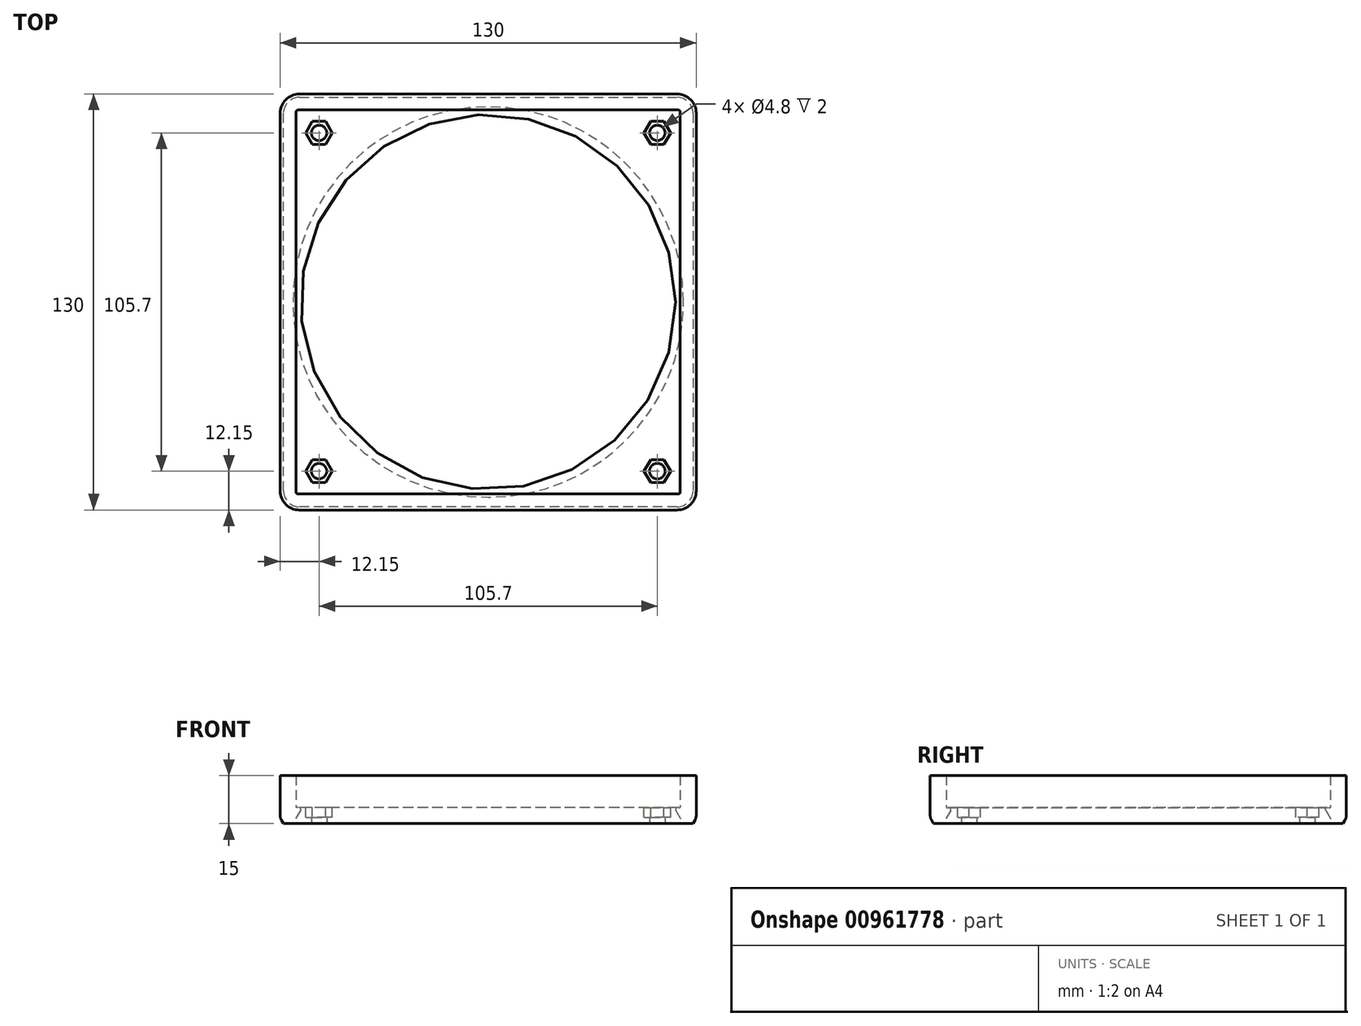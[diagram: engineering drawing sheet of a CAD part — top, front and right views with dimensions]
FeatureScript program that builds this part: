
annotation { "Feature Type Name" : "Feature", "Feature Type Description" : "" }
export const myFeature = defineFeature(function(context is Context, id is Id, definition is map)
    precondition{}
    {
        {
            var Q0;
            Q0=qCreatedBy(makeId("Top.planeOp"),FACE);
            var sketch = newSketch(context, id + "F0", { "sketchPlane" : qUnion([Q0])});
            skLineSegment(sketch, "E0.bottom", {"start": v(60, -60) * mm, "end": v(-60, -60) * mm});
            skLineSegment(sketch, "E0.top", {"start": v(60, 60) * mm, "end": v(-60, 60) * mm});
            skLineSegment(sketch, "E0.left", {"start": v(60, -60) * mm, "end": v(60, 60) * mm});
            skLineSegment(sketch, "E0.right", {"start": v(-60, -60) * mm, "end": v(-60, 60) * mm});
            skPoint(sketch, "E0.middle", {"position": v(0, 0) * mm});
            skLineSegment(sketch, "E1.0", {"start": v(65, -60) * mm, "end": v(65, 65) * mm});
            skLineSegment(sketch, "E1.1", {"start": v(65, 65) * mm, "end": v(-65, 65) * mm});
            skLineSegment(sketch, "E1.2", {"start": v(-65, -60) * mm, "end": v(-65, 65) * mm});
            skCircle(sketch, "E2", {"center": v(0, 0) * mm, "radius": 58 * mm});
            skLineSegment(sketch, "E3.bottom", {"start": v(52.85, 52.85) * mm, "end": v(-52.85, 52.85) * mm, "construction": true});
            skLineSegment(sketch, "E3.top", {"start": v(52.85, -52.85) * mm, "end": v(-52.85, -52.85) * mm, "construction": true});
            skLineSegment(sketch, "E3.left", {"start": v(52.85, 52.85) * mm, "end": v(52.85, -52.85) * mm, "construction": true});
            skLineSegment(sketch, "E3.right", {"start": v(-52.85, 52.85) * mm, "end": v(-52.85, -52.85) * mm, "construction": true});
            skCircle(sketch, "E4", {"center": v(-52.85, 52.85) * mm, "radius": 2 * mm});
            skCircle(sketch, "E5.0.1.0", {"center": v(-52.85, -52.85) * mm, "radius": 2 * mm});
            skCircle(sketch, "E5.1.0.0", {"center": v(52.85, 52.85) * mm, "radius": 2 * mm});
            skCircle(sketch, "E5.1.1.0", {"center": v(52.85, -52.85) * mm, "radius": 2 * mm});
            skLineSegment(sketch, "E5.direction1", {"start": v(-52.85, 52.85) * mm, "end": v(52.85, 52.85) * mm, "construction": true});
            skLineSegment(sketch, "E6.bottom", {"start": v(-60, -60) * mm, "end": v(60, -60) * mm});
            skLineSegment(sketch, "E6.top", {"start": v(-65, -65) * mm, "end": v(65, -65) * mm});
            skLineSegment(sketch, "E7.left", {"start": v(65, -65) * mm, "end": v(65, -71.7) * mm});
            skPoint(sketch, "E8.top.end.orphan", {"position": v(-74.22, -65) * mm});
            skLineSegment(sketch, "E9", {"start": v(-65, -60) * mm, "end": v(-65, -65) * mm});
            skLineSegment(sketch, "E10", {"start": v(65, -65) * mm, "end": v(65, -60) * mm});
            skSolve(sketch);
        }
        {
            var Q0;
            Q0=makeQuery(id+"F0.imprint","IMPRINT",FACE,{"disambiguationData":[TD([[makeQuery(id+"F0.imprint","IMPRINT",EDGE,{"derivedFrom":sQuery(id+"F0.wireOp",EDGE,"E4")}),1.0]])]});
            var Q1;
            Q1=makeQuery(id+"F0.imprint","IMPRINT",FACE,{"disambiguationData":[TD([[makeQuery(id+"F0.imprint","IMPRINT",EDGE,{"derivedFrom":sQuery(id+"F0.wireOp",EDGE,"E5.1.0.0")}),1.0]])]});
            var Q2;
            Q2=makeQuery(id+"F0.imprint","IMPRINT",FACE,{"disambiguationData":[TD([[makeQuery(id+"F0.imprint","IMPRINT",EDGE,{"derivedFrom":sQuery(id+"F0.wireOp",EDGE,"E5.1.1.0")}),1.0]])]});
            var Q3;
            Q3=makeQuery(id+"F0.imprint","IMPRINT",FACE,{"disambiguationData":[TD([[makeQuery(id+"F0.imprint","IMPRINT",EDGE,{"derivedFrom":sQuery(id+"F0.wireOp",EDGE,"E5.0.1.0")}),1.0]])]});
            var Q4;
            Q4=makeQuery(id+"F0.imprint","IMPRINT",FACE,{"disambiguationData":[TD([[makeQuery(id+"F0.imprint","IMPRINT",EDGE,{"derivedFrom":sQuery(id+"F0.wireOp",EDGE,"E0.top")}),1.0]])]});
            extrude(context, id + "F1", {"entities" : qUnion([Q0, Q1, Q2, Q3, Q4]), "depth" : 5 * mm, "offsetDistance" : 25 * mm});
        }
        {
            var Q0;
            Q0=makeQuery(id+"F0.imprint","IMPRINT",FACE,{"disambiguationData":[TD([[makeQuery(id+"F0.imprint","IMPRINT",EDGE,{"derivedFrom":sQuery(id+"F0.wireOp",EDGE,"E0.top")}),-1.0]])]});
            var Q1;
            Q1 = qSketchRegion(id + "F4", true);
            extrude(context, id + "F2", {"entities" : qUnion([Q0, Q1]), "operationType" : NewBodyOperationType.ADD, "depth" : 15 * mm, "offsetDistance" : 25 * mm});
        }
        {
            var Q0;
            Q0=sQuery(id+"F0.wireOp",VERTEX,"E3.top.start");
            var Q1;
            Q1=sQuery(id+"F0.wireOp",VERTEX,"E3.bottom.start");
            var Q2;
            Q2=sQuery(id+"F0.wireOp",VERTEX,"E3.bottom.end");
            var Q3;
            Q3=sQuery(id+"F0.wireOp",VERTEX,"E3.top.end");
            var Q4;
            Q4=makeQuery(id+"F1.opExtrude","SWEPT_BODY",BODY,{"disambiguationData":[OSD([sQuery(id+"F0.wireOp",EDGE,"E0.top"),sQuery(id+"F0.wireOp",EDGE,"E0.left"),sQuery(id+"F0.wireOp",EDGE,"E0.right"),sQuery(id+"F0.wireOp",EDGE,"E2"),sQuery(id+"F0.wireOp",EDGE,"E6.bottom")])]});
            hole(context, id + "F3", {"style" : HoleStyle.SIMPLE, "endStyle" : HoleEndStyle.BLIND, "oppositeDirection" : true, "standardTappedOrClearance" : lookupTablePath({ "fit" : "Loose", "standard" : "ISO", "size" : "M4", "type" : "Clearance" }), "standardBlindInLast" : lookupTablePath({ "fit" : "Loose", "standard" : "ISO", "engagement" : "75%", "pitch" : "0.7 mm", "size" : "M4", "type" : "Clearance & tapped" }), "holeDiameter" : 4.8 * mm, "majorDiameter" : 5 * mm, "holeDepth" : 4 * mm, "isTappedThrough" : true, "tappedDepth" : 12 * mm, "tapClearance" : 3, "locations" : qUnion([Q0, Q1, Q2, Q3]), "scope" : qUnion([Q4])});
        }
        {
            var Q0;
            Q0=makeQuery(id+"F1.opExtrude","CAP_FACE",FACE,{"disambiguationData":[OSD([sQuery(id+"F0.wireOp",EDGE,"E0.top"),sQuery(id+"F0.wireOp",EDGE,"E0.left"),sQuery(id+"F0.wireOp",EDGE,"E0.right"),sQuery(id+"F0.wireOp",EDGE,"E2"),sQuery(id+"F0.wireOp",EDGE,"E6.bottom")])],"isStart":false});
            var sketch = newSketch(context, id + "F4", { "sketchPlane" : qUnion([Q0])});
            skCircle(sketch, "E11.cCircle", {"center": v(-52.85, 52.85) * mm, "radius": 3.6 * mm, "construction": true});
            skLineSegment(sketch, "E11.0", {"start": v(-50.77, 49.25) * mm, "end": v(-54.93, 49.25) * mm});
            skLineSegment(sketch, "E11.1", {"start": v(-54.93, 49.25) * mm, "end": v(-57, 52.85) * mm});
            skLineSegment(sketch, "E11.2", {"start": v(-57, 52.85) * mm, "end": v(-54.93, 56.45) * mm});
            skLineSegment(sketch, "E11.3", {"start": v(-54.93, 56.45) * mm, "end": v(-50.77, 56.45) * mm});
            skLineSegment(sketch, "E11.4", {"start": v(-50.77, 56.45) * mm, "end": v(-48.7, 52.85) * mm});
            skLineSegment(sketch, "E11.5", {"start": v(-48.7, 52.85) * mm, "end": v(-50.77, 49.25) * mm});
            skPoint(sketch, "E11.0.midPoint", {"position": v(-52.85, 49.25) * mm});
            skLineSegment(sketch, "E12.0.1.0", {"start": v(-54.93, -49.25) * mm, "end": v(-50.77, -49.25) * mm});
            skLineSegment(sketch, "E12.0.1.1", {"start": v(-50.77, -49.25) * mm, "end": v(-48.7, -52.85) * mm});
            skLineSegment(sketch, "E12.0.1.2", {"start": v(-48.7, -52.85) * mm, "end": v(-50.77, -56.45) * mm});
            skLineSegment(sketch, "E12.0.1.3", {"start": v(-50.77, -56.45) * mm, "end": v(-54.93, -56.45) * mm});
            skLineSegment(sketch, "E12.0.1.4", {"start": v(-54.93, -56.45) * mm, "end": v(-57, -52.85) * mm});
            skLineSegment(sketch, "E12.0.1.5", {"start": v(-57, -52.85) * mm, "end": v(-54.93, -49.25) * mm});
            skLineSegment(sketch, "E12.1.0.0", {"start": v(50.77, 56.45) * mm, "end": v(54.93, 56.45) * mm});
            skLineSegment(sketch, "E12.1.0.1", {"start": v(54.93, 56.45) * mm, "end": v(57, 52.85) * mm});
            skLineSegment(sketch, "E12.1.0.2", {"start": v(57, 52.85) * mm, "end": v(54.93, 49.25) * mm});
            skLineSegment(sketch, "E12.1.0.3", {"start": v(54.93, 49.25) * mm, "end": v(50.77, 49.25) * mm});
            skLineSegment(sketch, "E12.1.0.4", {"start": v(50.77, 49.25) * mm, "end": v(48.7, 52.85) * mm});
            skLineSegment(sketch, "E12.1.0.5", {"start": v(48.7, 52.85) * mm, "end": v(50.77, 56.45) * mm});
            skLineSegment(sketch, "E12.1.1.0", {"start": v(50.77, -49.25) * mm, "end": v(54.93, -49.25) * mm});
            skLineSegment(sketch, "E12.1.1.1", {"start": v(54.93, -49.25) * mm, "end": v(57, -52.85) * mm});
            skLineSegment(sketch, "E12.1.1.2", {"start": v(57, -52.85) * mm, "end": v(54.93, -56.45) * mm});
            skLineSegment(sketch, "E12.1.1.3", {"start": v(54.93, -56.45) * mm, "end": v(50.77, -56.45) * mm});
            skLineSegment(sketch, "E12.1.1.4", {"start": v(50.77, -56.45) * mm, "end": v(48.7, -52.85) * mm});
            skLineSegment(sketch, "E12.1.1.5", {"start": v(48.7, -52.85) * mm, "end": v(50.77, -49.25) * mm});
            skLineSegment(sketch, "E12.direction1", {"start": v(-54.93, 56.45) * mm, "end": v(50.77, 56.45) * mm, "construction": true});
            skLineSegment(sketch, "E12.direction2", {"start": v(-54.93, 56.45) * mm, "end": v(-54.93, -49.25) * mm, "construction": true});
            skSolve(sketch);
        }
        {
            var Q0;
            Q0 = qSketchRegion(id + "F4", true);
            extrude(context, id + "F5", {"entities" : qUnion([Q0]), "operationType" : NewBodyOperationType.REMOVE, "oppositeDirection" : true, "depth" : 3 * mm, "offsetDistance" : 25 * mm});
        }
        {
            var Q0;
            Q0=makeQuery(id+"F1.opExtrude","CAP_EDGE",EDGE,{"disambiguationData":[OSD([sQuery(id+"F0.wireOp",EDGE,"E2")])],"isStart":true});
            chamfer(context, id + "F6", {"entities" : qUnion([Q0]), "chamferType" : ChamferType.OFFSET_ANGLE, "width" : 3 * mm, "oppositeDirection" : false, "angle" : 60 * degree, "tangentPropagation" : true});
        }
        {
            var Q0;
            Q0=makeQuery(id+"F2.opExtrude","SWEPT_EDGE",EDGE,{"disambiguationData":[OSD([sQuery(id+"F0.wireOp",EDGE,"E0.top"),sQuery(id+"F0.wireOp",EDGE,"E0.left")])]});
            var Q1;
            Q1=makeQuery(id+"F2.opExtrude","SWEPT_EDGE",EDGE,{"disambiguationData":[OSD([sQuery(id+"F0.wireOp",EDGE,"E0.top"),sQuery(id+"F0.wireOp",EDGE,"E0.right")])]});
            var Q2;
            Q2=makeQuery(id+"F2.opExtrude","SWEPT_EDGE",EDGE,{"disambiguationData":[OSD([sQuery(id+"F0.wireOp",EDGE,"E0.right"),sQuery(id+"F0.wireOp",EDGE,"E6.bottom")])]});
            var Q3;
            Q3=makeQuery(id+"F2.opExtrude","SWEPT_EDGE",EDGE,{"disambiguationData":[OSD([sQuery(id+"F0.wireOp",EDGE,"E0.left"),sQuery(id+"F0.wireOp",EDGE,"E6.bottom")])]});
            var Q4;
            Q4=makeQuery(id+"F1.opExtrude","CAP_EDGE",EDGE,{"disambiguationData":[OSD([sQuery(id+"F0.wireOp",EDGE,"E6.bottom")])],"isStart":false});
            var Q5;
            Q5=makeQuery(id+"F1.opExtrude","CAP_EDGE",EDGE,{"disambiguationData":[OSD([sQuery(id+"F0.wireOp",EDGE,"E0.left")])],"isStart":false});
            var Q6;
            Q6=makeQuery(id+"F1.opExtrude","CAP_EDGE",EDGE,{"disambiguationData":[OSD([sQuery(id+"F0.wireOp",EDGE,"E0.right")])],"isStart":false});
            var Q7;
            Q7=makeQuery(id+"F1.opExtrude","CAP_EDGE",EDGE,{"disambiguationData":[OSD([sQuery(id+"F0.wireOp",EDGE,"E0.top")])],"isStart":false});
            var Q8;
            {var subQ0=sQuery(id+"F0.wireOp",EDGE,"E2");Q8=makeQuery(id+"F6.opChamfer","BLEND_EDGE",EDGE,{"blendedFrom":[makeQuery(id+"F1.opExtrude","CAP_EDGE",EDGE,{"disambiguationData":[OSD([subQ0])],"isStart":true}),makeQuery(id+"F1.opExtrude","CAP_FACE",FACE,{"disambiguationData":[OSD([sQuery(id+"F0.wireOp",EDGE,"E0.top"),sQuery(id+"F0.wireOp",EDGE,"E0.left"),sQuery(id+"F0.wireOp",EDGE,"E0.right"),subQ0,sQuery(id+"F0.wireOp",EDGE,"E6.bottom")])],"isStart":false})],"blendedInto":[makeQuery(id+"F1.opExtrude","CAP_FACE",FACE,{"disambiguationData":[OSD([sQuery(id+"F0.wireOp",EDGE,"E0.top"),sQuery(id+"F0.wireOp",EDGE,"E0.left"),sQuery(id+"F0.wireOp",EDGE,"E0.right"),subQ0,sQuery(id+"F0.wireOp",EDGE,"E6.bottom")])],"isStart":false})]});}
            fillet(context, id + "F7", {"entities" : qUnion([Q0, Q1, Q2, Q3, Q4, Q5, Q6, Q7, Q8]), "tangentPropagation" : true, "radius" : 0.6 * mm, "defaultsChanged" : true, "vertexSettings" : [], "allowEdgeOverflow" : false});
        }
        {
            var Q0;
            Q0=makeQuery(id+"F2.opExtrude","SWEPT_EDGE",EDGE,{"disambiguationData":[OSD([sQuery(id+"F0.wireOp",EDGE,"E6.top"),sQuery(id+"F0.wireOp",EDGE,"E10")])]});
            var Q1;
            Q1=makeQuery(id+"F2.opExtrude","SWEPT_EDGE",EDGE,{"disambiguationData":[OSD([sQuery(id+"F0.wireOp",EDGE,"E1.0"),sQuery(id+"F0.wireOp",EDGE,"E1.1")])]});
            var Q2;
            Q2=makeQuery(id+"F2.opExtrude","SWEPT_EDGE",EDGE,{"disambiguationData":[OSD([sQuery(id+"F0.wireOp",EDGE,"E1.1"),sQuery(id+"F0.wireOp",EDGE,"E1.2")])]});
            var Q3;
            Q3=makeQuery(id+"F2.opExtrude","SWEPT_EDGE",EDGE,{"disambiguationData":[OSD([sQuery(id+"F0.wireOp",EDGE,"E6.top"),sQuery(id+"F0.wireOp",EDGE,"E9")])]});
            fillet(context, id + "F8", {"entities" : qUnion([Q0, Q1, Q2, Q3]), "tangentPropagation" : true, "radius" : 6 * mm, "defaultsChanged" : false, "vertexSettings" : [], "allowEdgeOverflow" : false});
        }
        {
            var Q0;
            {var subQ0=sQuery(id+"F0.wireOp",EDGE,"E6.bottom");var subQ1=sQuery(id+"F0.wireOp",EDGE,"E1.2");var subQ2=sQuery(id+"F0.wireOp",EDGE,"E1.1");var subQ3=sQuery(id+"F0.wireOp",EDGE,"E0.right");var subQ4=sQuery(id+"F0.wireOp",EDGE,"E0.left");var subQ5=sQuery(id+"F0.wireOp",EDGE,"E0.top");Q0=makeQuery(id+"F8.opFillet","BLEND_EDGE",EDGE,{"blendedFrom":[makeQuery(id+"F2.opExtrude","SWEPT_EDGE",EDGE,{"disambiguationData":[OSD([subQ2,subQ1])]}),makeQuery(id+"F2.boolean.opBoolean","MERGE",FACE,{"derivedFrom":[makeQuery(id+"F1.opExtrude","CAP_FACE",FACE,{"disambiguationData":[OSD([subQ5,subQ4,subQ3,sQuery(id+"F0.wireOp",EDGE,"E2"),subQ0])],"isStart":true}),makeQuery(id+"F2.opExtrude","CAP_FACE",FACE,{"disambiguationData":[OSD([subQ5,subQ4,subQ3,sQuery(id+"F0.wireOp",EDGE,"E1.0"),subQ2,subQ1,subQ0,sQuery(id+"F0.wireOp",EDGE,"E6.top"),sQuery(id+"F0.wireOp",EDGE,"E9"),sQuery(id+"F0.wireOp",EDGE,"E10")])],"isStart":true})]})],"blendedInto":[makeQuery(id+"F2.boolean.opBoolean","MERGE",FACE,{"derivedFrom":[makeQuery(id+"F1.opExtrude","CAP_FACE",FACE,{"disambiguationData":[OSD([subQ5,subQ4,subQ3,sQuery(id+"F0.wireOp",EDGE,"E2"),subQ0])],"isStart":true}),makeQuery(id+"F2.opExtrude","CAP_FACE",FACE,{"disambiguationData":[OSD([subQ5,subQ4,subQ3,sQuery(id+"F0.wireOp",EDGE,"E1.0"),subQ2,subQ1,subQ0,sQuery(id+"F0.wireOp",EDGE,"E6.top"),sQuery(id+"F0.wireOp",EDGE,"E9"),sQuery(id+"F0.wireOp",EDGE,"E10")])],"isStart":true})]})]});}
            chamfer(context, id + "F9", {"entities" : qUnion([Q0]), "chamferType" : ChamferType.OFFSET_ANGLE, "width" : 1 * mm, "oppositeDirection" : false, "angle" : 60 * degree, "tangentPropagation" : true});
        }
        {
            var Q0;
            {var subQ0=sQuery(id+"F0.wireOp",EDGE,"E1.2");var subQ1=sQuery(id+"F0.wireOp",EDGE,"E1.1");var subQ2=sQuery(id+"F0.wireOp",EDGE,"E6.bottom");var subQ3=sQuery(id+"F0.wireOp",EDGE,"E0.right");var subQ4=sQuery(id+"F0.wireOp",EDGE,"E0.left");var subQ5=sQuery(id+"F0.wireOp",EDGE,"E0.top");Q0=makeQuery(id+"F9.opChamfer","BLEND_EDGE",EDGE,{"blendedFrom":[makeQuery(id+"F8.opFillet","BLEND_EDGE",EDGE,{"blendedFrom":[makeQuery(id+"F2.opExtrude","SWEPT_EDGE",EDGE,{"disambiguationData":[OSD([subQ1,subQ0])]}),makeQuery(id+"F2.boolean.opBoolean","MERGE",FACE,{"derivedFrom":[makeQuery(id+"F1.opExtrude","CAP_FACE",FACE,{"disambiguationData":[OSD([subQ5,subQ4,subQ3,sQuery(id+"F0.wireOp",EDGE,"E2"),subQ2])],"isStart":true}),makeQuery(id+"F2.opExtrude","CAP_FACE",FACE,{"disambiguationData":[OSD([subQ5,subQ4,subQ3,sQuery(id+"F0.wireOp",EDGE,"E1.0"),subQ1,subQ0,subQ2,sQuery(id+"F0.wireOp",EDGE,"E6.top"),sQuery(id+"F0.wireOp",EDGE,"E9"),sQuery(id+"F0.wireOp",EDGE,"E10")])],"isStart":true})]})],"blendedInto":[makeQuery(id+"F2.boolean.opBoolean","MERGE",FACE,{"derivedFrom":[makeQuery(id+"F1.opExtrude","CAP_FACE",FACE,{"disambiguationData":[OSD([subQ5,subQ4,subQ3,sQuery(id+"F0.wireOp",EDGE,"E2"),subQ2])],"isStart":true}),makeQuery(id+"F2.opExtrude","CAP_FACE",FACE,{"disambiguationData":[OSD([subQ5,subQ4,subQ3,sQuery(id+"F0.wireOp",EDGE,"E1.0"),subQ1,subQ0,subQ2,sQuery(id+"F0.wireOp",EDGE,"E6.top"),sQuery(id+"F0.wireOp",EDGE,"E9"),sQuery(id+"F0.wireOp",EDGE,"E10")])],"isStart":true})]})]}),makeQuery(id+"F8.opFillet","BLEND_FACE",FACE,{"disambiguationData":[OSD([subQ1,subQ0])]})],"blendedInto":[makeQuery(id+"F8.opFillet","BLEND_FACE",FACE,{"disambiguationData":[OSD([subQ1,subQ0])]})]});}
            fillet(context, id + "F10", {"entities" : qUnion([Q0]), "tangentPropagation" : true, "radius" : 3 * mm, "defaultsChanged" : true, "vertexSettings" : [], "allowEdgeOverflow" : false});
        }
    });
